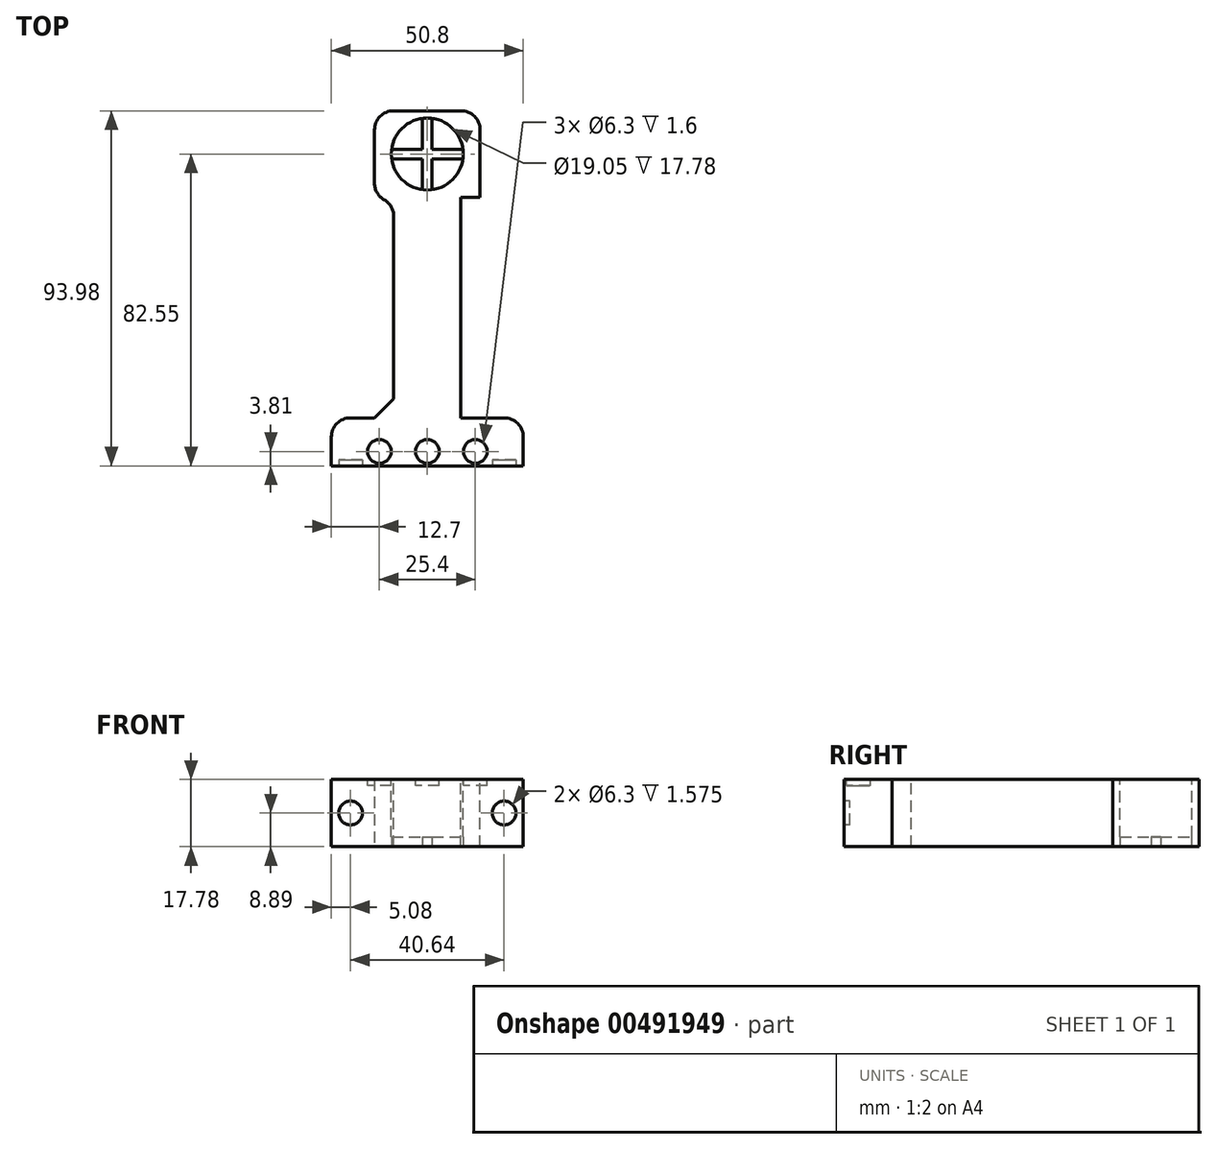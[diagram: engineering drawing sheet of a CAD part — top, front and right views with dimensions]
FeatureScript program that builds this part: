
annotation { "Feature Type Name" : "Feature", "Feature Type Description" : "" }
export const myFeature = defineFeature(function(context is Context, id is Id, definition is map)
    precondition{}
    {
        {
            var Q0;
            Q0=qCreatedBy(makeId("Front.planeOp"),FACE);
            var sketch = newSketch(context, id + "F0", { "sketchPlane" : qUnion([Q0])});
            skLineSegment(sketch, "E0.bottom", {"start": v(25.4, 8.9) * mm, "end": v(-25.4, 8.9) * mm});
            skLineSegment(sketch, "E0.top", {"start": v(25.4, -8.9) * mm, "end": v(-25.4, -8.9) * mm});
            skLineSegment(sketch, "E0.left", {"start": v(25.4, 8.9) * mm, "end": v(25.4, -8.9) * mm});
            skLineSegment(sketch, "E0.right", {"start": v(-25.4, 8.9) * mm, "end": v(-25.4, -8.9) * mm});
            skPoint(sketch, "E0.middle", {"position": v(0, 0) * mm});
            skSolve(sketch);
        }
        {
            var Q0;
            Q0 = qSketchRegion(id + "F0", true);
            extrude(context, id + "F1", {"entities" : qUnion([Q0]), "depth" : 12.7 * mm});
        }
        {
            var Q0;
            Q0=makeQuery(id+"F1.opExtrude","CAP_FACE",FACE,{"disambiguationData":[OSD([sQuery(id+"F0.wireOp",EDGE,"E0.bottom"),sQuery(id+"F0.wireOp",EDGE,"E0.top"),sQuery(id+"F0.wireOp",EDGE,"E0.left"),sQuery(id+"F0.wireOp",EDGE,"E0.right")])],"isStart":true});
            var sketch = newSketch(context, id + "F2", { "sketchPlane" : qUnion([Q0])});
            skLineSegment(sketch, "E1.bottom", {"start": v(8.9, -8.89) * mm, "end": v(-8.89, -8.9) * mm});
            skLineSegment(sketch, "E1.top", {"start": v(8.9, 8.9) * mm, "end": v(-8.89, 8.9) * mm});
            skLineSegment(sketch, "E1.left", {"start": v(8.9, -8.89) * mm, "end": v(8.9, 8.9) * mm});
            skLineSegment(sketch, "E1.right", {"start": v(-8.89, -8.9) * mm, "end": v(-8.89, 8.9) * mm});
            skPoint(sketch, "E1.middle", {"position": v(0, 0) * mm});
            skSolve(sketch);
        }
        {
            var Q0;
            Q0 = qSketchRegion(id + "F2", true);
            extrude(context, id + "F3", {"entities" : qUnion([Q0]), "operationType" : NewBodyOperationType.ADD, "depth" : 58.42 * mm});
        }
        {
            var Q0;
            Q0=makeQuery(id+"F3.opExtrude","SWEPT_FACE",FACE,{"disambiguationData":[OSD([sQuery(id+"F2.wireOp",EDGE,"E1.top")])]});
            var sketch = newSketch(context, id + "F4", { "sketchPlane" : qUnion([Q0])});
            skLineSegment(sketch, "E2.0", {"start": v(-8.9, 58.42) * mm, "end": v(8.89, 58.42) * mm});
            skLineSegment(sketch, "E3", {"start": v(-8.9, 58.42) * mm, "end": v(-13.97, 58.42) * mm});
            skLineSegment(sketch, "E4", {"start": v(8.89, 58.42) * mm, "end": v(13.97, 58.42) * mm});
            skLineSegment(sketch, "E5", {"start": v(-13.97, 58.42) * mm, "end": v(-13.97, 81.28) * mm});
            skLineSegment(sketch, "E6", {"start": v(-13.97, 81.28) * mm, "end": v(13.97, 81.28) * mm});
            skLineSegment(sketch, "E7", {"start": v(13.97, 81.28) * mm, "end": v(13.97, 58.42) * mm});
            skCircle(sketch, "E8", {"center": v(0, 69.85) * mm, "radius": 9.53 * mm});
            skSolve(sketch);
        }
        {
            var Q0;
            Q0 = qSketchRegion(id + "F4", true);
            var Q1;
            Q1=makeQuery(id+"F3.opExtrude","SWEPT_FACE",FACE,{"disambiguationData":[OSD([sQuery(id+"F2.wireOp",EDGE,"E1.bottom")])]});
            extrude(context, id + "F5", {"entities" : qUnion([Q0]), "operationType" : NewBodyOperationType.ADD, "endBound" : BoundingType.UP_TO_SURFACE, "oppositeDirection" : true, "endBoundEntityFace" : qUnion([Q1]), "depth" : 25.4 * mm});
        }
        {
            var Q0;
            {var subQ0=sQuery(id+"F2.wireOp",EDGE,"E1.bottom");Q0=makeQuery(id+"F5.boolean.opBoolean","MERGE",FACE,{"derivedFrom":[makeQuery(id+"F3.opExtrude","SWEPT_FACE",FACE,{"disambiguationData":[OSD([subQ0])]}),makeQuery(id+"F5.opExtrude","CAP_FACE",FACE,{"disambiguationData":[OSD([subQ0])],"isStart":false})]});}
            var sketch = newSketch(context, id + "F6", { "sketchPlane" : qUnion([Q0])});
            skArc(sketch, "E9.0", {"start": v(9.44, -71.12) * mm, "mid": v(9.52, -69.85) * mm, "end": v(9.44, -68.58) * mm});
            skLineSegment(sketch, "E10.left", {"start": v(-1.27, -60.41) * mm, "end": v(-1.27, -68.58) * mm});
            skLineSegment(sketch, "E10.right", {"start": v(1.27, -60.41) * mm, "end": v(1.27, -68.58) * mm});
            skPoint(sketch, "E10.bottom.start.orphan", {"position": v(-1.27, -58.25) * mm});
            skPoint(sketch, "E11.orphan", {"position": v(1.27, -58.25) * mm});
            skLineSegment(sketch, "E12.bottom", {"start": v(-9.44, -68.58) * mm, "end": v(-1.27, -68.58) * mm});
            skLineSegment(sketch, "E12.top", {"start": v(-9.44, -71.12) * mm, "end": v(-1.27, -71.12) * mm});
            skPoint(sketch, "E12.left.end.orphan", {"position": v(-12.4, -71.12) * mm});
            skPoint(sketch, "E12.left.start.orphan", {"position": v(-12.4, -68.58) * mm});
            skPoint(sketch, "E13.orphan", {"position": v(12.4, -71.12) * mm});
            skPoint(sketch, "E14.orphan", {"position": v(12.4, -68.58) * mm});
            skPoint(sketch, "E10.top.end.orphan", {"position": v(1.27, -81.45) * mm});
            skPoint(sketch, "E15.orphan", {"position": v(-1.27, -81.45) * mm});
            skArc(sketch, "E16.trimOffspring", {"start": v(-1.27, -79.29) * mm, "mid": v(0, -79.38) * mm, "end": v(1.27, -79.29) * mm});
            skArc(sketch, "E17.trimOffspring", {"start": v(-9.44, -68.58) * mm, "mid": v(-9.53, -69.85) * mm, "end": v(-9.44, -71.12) * mm});
            skArc(sketch, "E18.trimOffspring", {"start": v(1.27, -60.41) * mm, "mid": v(0, -60.32) * mm, "end": v(-1.27, -60.41) * mm});
            skLineSegment(sketch, "E19.trimOffspring", {"start": v(1.27, -68.58) * mm, "end": v(9.44, -68.58) * mm});
            skLineSegment(sketch, "E20.trimOffspring", {"start": v(1.27, -71.12) * mm, "end": v(9.44, -71.12) * mm});
            skLineSegment(sketch, "E21.trimOffspring", {"start": v(1.27, -71.12) * mm, "end": v(1.27, -79.29) * mm});
            skLineSegment(sketch, "E22.trimOffspring", {"start": v(-1.27, -71.12) * mm, "end": v(-1.27, -79.29) * mm});
            skSolve(sketch);
        }
        {
            var Q0;
            Q0 = qSketchRegion(id + "F6", true);
            extrude(context, id + "F7", {"entities" : qUnion([Q0]), "operationType" : NewBodyOperationType.ADD, "oppositeDirection" : true, "depth" : 2.54 * mm});
        }
        {
            var Q0;
            Q0=makeQuery(id+"F3.opExtrude","CAP_EDGE",EDGE,{"disambiguationData":[OSD([sQuery(id+"F2.wireOp",EDGE,"E1.left")])],"isStart":false});
            var Q1;
            Q1=makeQuery(id+"F3.opExtrude","CAP_EDGE",EDGE,{"disambiguationData":[OSD([sQuery(id+"F2.wireOp",EDGE,"E1.right")])],"isStart":false});
            fillet(context, id + "F8", {"entities" : qUnion([Q0, Q1]), "radius" : 5.08 * mm, "tangentPropagation" : true, "allowEdgeOverflow" : false});
        }
        {
            var Q0;
            Q0=makeQuery(id+"F5.opExtrude","SWEPT_EDGE",EDGE,{"disambiguationData":[OSD([sQuery(id+"F4.wireOp",EDGE,"E5"),sQuery(id+"F4.wireOp",EDGE,"E6")])]});
            var Q1;
            Q1=makeQuery(id+"F5.opExtrude","SWEPT_EDGE",EDGE,{"disambiguationData":[OSD([sQuery(id+"F4.wireOp",EDGE,"E6"),sQuery(id+"F4.wireOp",EDGE,"E7")])]});
            fillet(context, id + "F9", {"entities" : qUnion([Q0, Q1]), "radius" : 5.08 * mm, "tangentPropagation" : true, "allowEdgeOverflow" : false});
        }
        {
            var Q0;
            Q0=makeQuery(id+"F8.opFillet","BLEND_EDGE",EDGE,{"blendedFrom":[makeQuery(id+"F3.opExtrude","CAP_EDGE",EDGE,{"disambiguationData":[OSD([sQuery(id+"F2.wireOp",EDGE,"E1.left")])],"isStart":false}),makeQuery(id+"F5.opExtrude","SWEPT_FACE",FACE,{"disambiguationData":[OSD([sQuery(id+"F4.wireOp",EDGE,"E5")])]})],"blendedInto":[makeQuery(id+"F5.opExtrude","SWEPT_FACE",FACE,{"disambiguationData":[OSD([sQuery(id+"F4.wireOp",EDGE,"E5")])]})]});
            var Q1;
            Q1=makeQuery(id+"F8.opFillet","BLEND_EDGE",EDGE,{"blendedFrom":[makeQuery(id+"F3.opExtrude","CAP_EDGE",EDGE,{"disambiguationData":[OSD([sQuery(id+"F2.wireOp",EDGE,"E1.right")])],"isStart":false}),makeQuery(id+"F5.opExtrude","SWEPT_FACE",FACE,{"disambiguationData":[OSD([sQuery(id+"F4.wireOp",EDGE,"E7")])]})],"blendedInto":[makeQuery(id+"F5.opExtrude","SWEPT_FACE",FACE,{"disambiguationData":[OSD([sQuery(id+"F4.wireOp",EDGE,"E7")])]})]});
            fillet(context, id + "F10", {"entities" : qUnion([Q0, Q1]), "radius" : 5.08 * mm, "tangentPropagation" : true, "allowEdgeOverflow" : false});
        }
        {
            var Q0;
            Q0=makeQuery(id+"F1.opExtrude","CAP_FACE",FACE,{"disambiguationData":[OSD([sQuery(id+"F0.wireOp",EDGE,"E0.bottom"),sQuery(id+"F0.wireOp",EDGE,"E0.top"),sQuery(id+"F0.wireOp",EDGE,"E0.left"),sQuery(id+"F0.wireOp",EDGE,"E0.right")])],"isStart":false});
            var sketch = newSketch(context, id + "F11", { "sketchPlane" : qUnion([Q0])});
            skLineSegment(sketch, "E23.0.2", {"start": v(25.4, 8.9) * mm, "end": v(-25.4, 8.9) * mm});
            skPoint(sketch, "E24.endSnap0", {"position": v(-25.4, 0) * mm});
            skPoint(sketch, "E25.endSnap0", {"position": v(25.4, 0) * mm});
            skLineSegment(sketch, "E26", {"start": v(-25.4, 0) * mm, "end": v(-20.32, 0) * mm});
            skCircle(sketch, "E27", {"center": v(-20.32, 0) * mm, "radius": 3.15 * mm});
            skLineSegment(sketch, "E28", {"start": v(25.4, 0) * mm, "end": v(20.32, 0) * mm});
            skCircle(sketch, "E29", {"center": v(20.32, 0) * mm, "radius": 3.15 * mm});
            skSolve(sketch);
        }
        {
            var Q0;
            Q0 = qSketchRegion(id + "F11", true);
            extrude(context, id + "F12", {"entities" : qUnion([Q0]), "operationType" : NewBodyOperationType.REMOVE, "oppositeDirection" : true, "depth" : 1.57 * mm});
        }
        {
            var Q0;
            Q0=makeQuery(id+"F3.opExtrude","CAP_EDGE",EDGE,{"disambiguationData":[OSD([sQuery(id+"F2.wireOp",EDGE,"E1.left")])],"isStart":true});
            var Q1;
            Q1=makeQuery(id+"F3.opExtrude","CAP_EDGE",EDGE,{"disambiguationData":[OSD([sQuery(id+"F2.wireOp",EDGE,"E1.right")])],"isStart":true});
            chamfer(context, id + "F13", {"entities" : qUnion([Q0, Q1]), "width" : 5.08 * mm, "tangentPropagation" : true});
        }
        {
            var Q0;
            Q0=makeQuery(id+"F1.opExtrude","CAP_EDGE",EDGE,{"disambiguationData":[OSD([sQuery(id+"F0.wireOp",EDGE,"E0.right")])],"isStart":true});
            var Q1;
            Q1=makeQuery(id+"F1.opExtrude","CAP_EDGE",EDGE,{"disambiguationData":[OSD([sQuery(id+"F0.wireOp",EDGE,"E0.left")])],"isStart":true});
            fillet(context, id + "F14", {"entities" : qUnion([Q0, Q1]), "radius" : 5.08 * mm, "tangentPropagation" : true, "allowEdgeOverflow" : false});
        }
        {
            var Q0;
            Q0=makeQuery(id+"F5.boolean.opBoolean","MERGE",FACE,{"derivedFrom":[makeQuery(id+"F3.boolean.opBoolean","MERGE",FACE,{"derivedFrom":[makeQuery(id+"F1.opExtrude","SWEPT_FACE",FACE,{"disambiguationData":[OSD([sQuery(id+"F0.wireOp",EDGE,"E0.bottom")])]}),makeQuery(id+"F3.opExtrude","SWEPT_FACE",FACE,{"disambiguationData":[OSD([sQuery(id+"F2.wireOp",EDGE,"E1.top")])]})]}),makeQuery(id+"F5.opExtrude","CAP_FACE",FACE,{"disambiguationData":[OSD([sQuery(id+"F4.wireOp",EDGE,"E2.0"),sQuery(id+"F4.wireOp",EDGE,"E3"),sQuery(id+"F4.wireOp",EDGE,"E4"),sQuery(id+"F4.wireOp",EDGE,"E5"),sQuery(id+"F4.wireOp",EDGE,"E6"),sQuery(id+"F4.wireOp",EDGE,"E7"),sQuery(id+"F4.wireOp",EDGE,"E8")])],"isStart":true})]});
            var sketch = newSketch(context, id + "F15", { "sketchPlane" : qUnion([Q0])});
            skLineSegment(sketch, "E30.0", {"start": v(-25.4, -12.7) * mm, "end": v(-25.4, -5.08) * mm});
            skLineSegment(sketch, "E31.0", {"start": v(25.4, -12.7) * mm, "end": v(-25.4, -12.7) * mm});
            skLineSegment(sketch, "E32.0", {"start": v(25.4, -12.7) * mm, "end": v(25.4, -5.08) * mm});
            skLineSegment(sketch, "E33", {"start": v(0, -12.7) * mm, "end": v(0, -8.9) * mm});
            skPoint(sketch, "E33.endSnap0", {"position": v(-25.4, -8.9) * mm});
            skCircle(sketch, "E34", {"center": v(0, -8.9) * mm, "radius": 3.15 * mm});
            skLineSegment(sketch, "E35", {"start": v(0, -8.9) * mm, "end": v(12.7, -8.9) * mm});
            skLineSegment(sketch, "E36", {"start": v(0, -8.9) * mm, "end": v(-12.7, -8.9) * mm});
            skCircle(sketch, "E37", {"center": v(-12.7, -8.9) * mm, "radius": 3.15 * mm});
            skCircle(sketch, "E38", {"center": v(12.7, -8.9) * mm, "radius": 3.15 * mm});
            skSolve(sketch);
        }
        {
            var Q0;
            Q0 = qSketchRegion(id + "F15", true);
            extrude(context, id + "F16", {"entities" : qUnion([Q0]), "operationType" : NewBodyOperationType.REMOVE, "oppositeDirection" : true, "depth" : 1.6 * mm});
        }
    });
